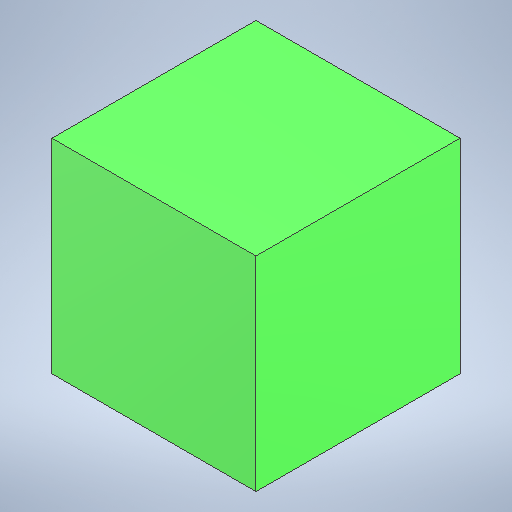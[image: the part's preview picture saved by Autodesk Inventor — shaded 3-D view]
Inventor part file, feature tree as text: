
AUTODESK INVENTOR PART (.ipt)
format: ipt  version: 2025.3 (Build 293356000, 356)  size: 180,736 bytes
history: native  units: mm
features: other x1, extrude x1, sketch x1
ambient origin geometry x8: Origin, YZ Plane, XZ Plane, XY Plane, X Axis, Y Axis, Z Axis, Center Point
bodies: Body1 (feature_tree)
feature tree (3):
  other  "Sólido1"
  extrude  "Extrusión1"  Depth=200.0mm
  sketch  "Boceto1"  dims[d0=200.0mm d1=200.0mm d2=200.0mm d3=0.0mm]
